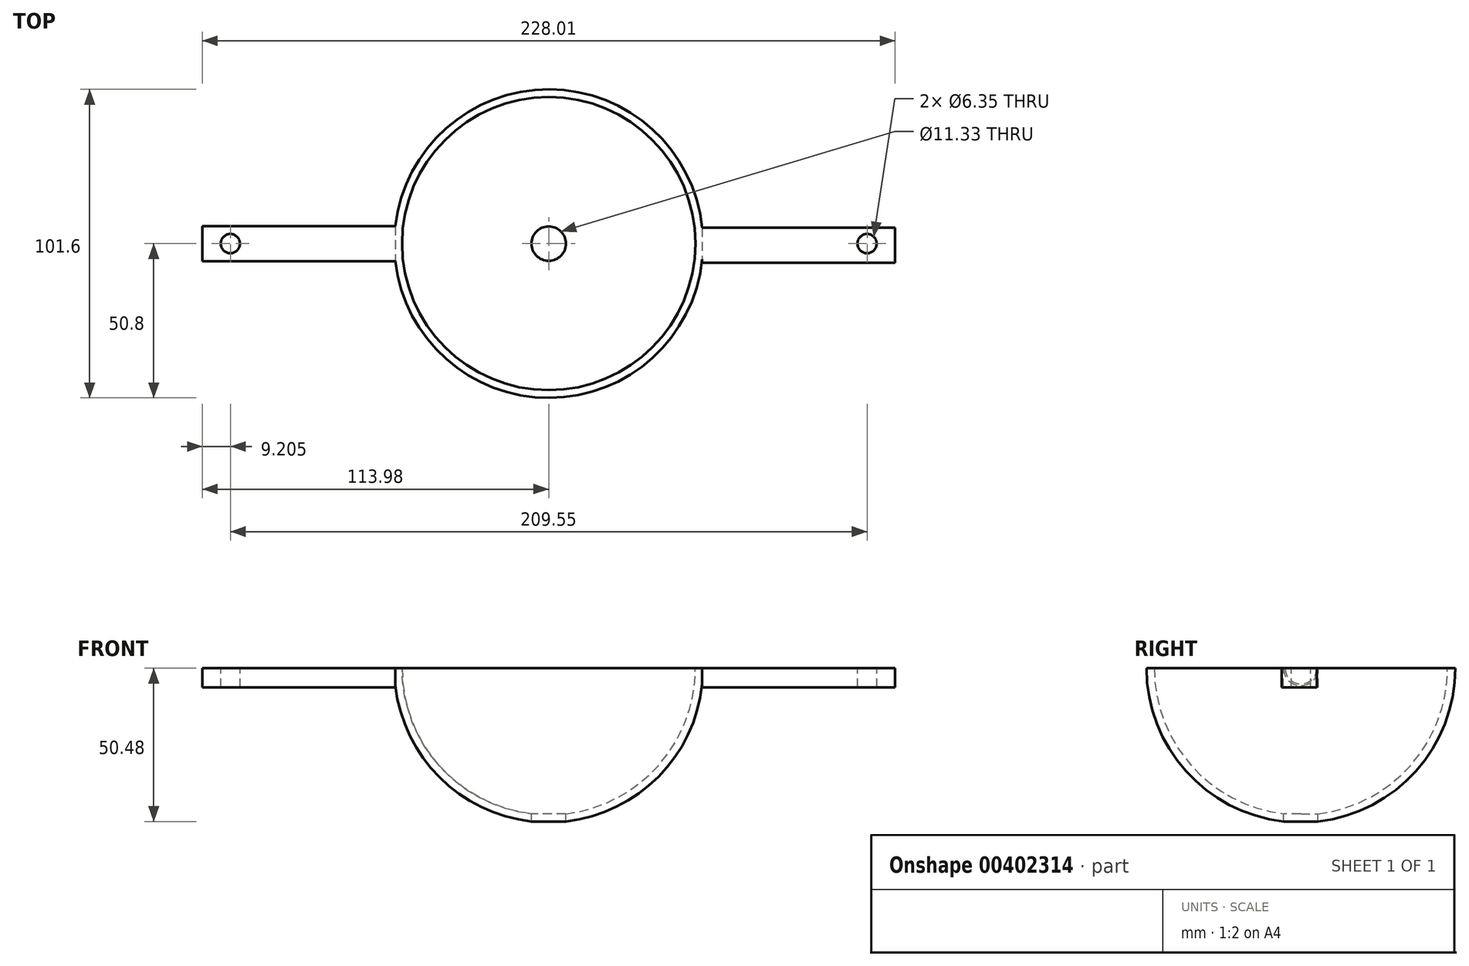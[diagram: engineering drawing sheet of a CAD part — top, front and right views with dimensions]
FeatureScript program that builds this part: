
annotation { "Feature Type Name" : "Feature", "Feature Type Description" : "" }
export const myFeature = defineFeature(function(context is Context, id is Id, definition is map)
    precondition{}
    {
        {
            var Q0;
            Q0=qCreatedBy(makeId("Front.planeOp"),FACE);
            var sketch = newSketch(context, id + "F0", { "sketchPlane" : qUnion([Q0])});
            skArc(sketch, "E0", {"start": v(-50.8, 0) * mm, "mid": v(-35.92, -35.92) * mm, "end": v(0, -50.8) * mm});
            skLineSegment(sketch, "E1", {"start": v(-50.8, 0) * mm, "end": v(0, 0) * mm});
            skLineSegment(sketch, "E2", {"start": v(0, 0) * mm, "end": v(0, -50.8) * mm});
            skPoint(sketch, "E3.orphan", {"position": v(50.8, 0) * mm});
            skSolve(sketch);
        }
        {
            var Q0;
            Q0 = qSketchRegion(id + "F0", true);
            var Q1;
            Q1=sQuery(id+"F0.wireOp",EDGE,"E2");
            revolve(context, id + "F1", {"entities" : qUnion([Q0]), "axis" : qUnion([Q1]), "revolveType" : RevolveType.FULL});
        }
        {
            var Q0;
            Q0=makeQuery(id+"F1.opRevolve","SWEPT_FACE",FACE,{"disambiguationData":[OSD([sQuery(id+"F0.wireOp",EDGE,"E1")])]});
            shell(context, id + "F2", {"entities" : qUnion([Q0]), "thickness" : 2.54 * mm});
        }
        {
            var Q0;
            Q0=qCreatedBy(makeId("Top.planeOp"),FACE);
            var sketch = newSketch(context, id + "F3", { "sketchPlane" : qUnion([Q0])});
            skCircle(sketch, "E4", {"center": v(0, 0) * mm, "radius": 5.67 * mm});
            skSolve(sketch);
        }
        {
            var Q0;
            Q0=makeQuery(id+"F3.imprint","IMPRINT",FACE,{"disambiguationData":[TD([[makeQuery(id+"F3.imprint","IMPRINT",EDGE,{"derivedFrom":sQuery(id+"F3.wireOp",EDGE,"E4")}),1.0]])]});
            extrude(context, id + "F4", {"entities" : qUnion([Q0]), "operationType" : NewBodyOperationType.REMOVE, "endBound" : BoundingType.THROUGH_ALL, "oppositeDirection" : true, "depth" : 25.4 * mm});
        }
        {
            var Q0;
            Q0=qCreatedBy(makeId("Top.planeOp"),FACE);
            var sketch = newSketch(context, id + "F5", { "sketchPlane" : qUnion([Q0])});
            skLineSegment(sketch, "E5.bottom", {"start": v(-50.48, 5.73) * mm, "end": v(-113.98, 5.73) * mm});
            skLineSegment(sketch, "E5.top", {"start": v(-50.48, -5.75) * mm, "end": v(-113.98, -5.75) * mm});
            skLineSegment(sketch, "E5.left", {"start": v(-50.48, 5.73) * mm, "end": v(-50.48, -5.75) * mm});
            skLineSegment(sketch, "E5.right", {"start": v(-113.98, 5.73) * mm, "end": v(-113.98, -5.75) * mm});
            skLineSegment(sketch, "E6", {"start": v(-113.98, 0) * mm, "end": v(-50.48, 0) * mm});
            skSolve(sketch);
        }
        {
            var Q0;
            Q0 = qSketchRegion(id + "F5", true);
            extrude(context, id + "F6", {"entities" : qUnion([Q0]), "operationType" : NewBodyOperationType.ADD, "oppositeDirection" : true, "depth" : 6.35 * mm});
        }
        {
            var Q0;
            Q0=qCreatedBy(makeId("Top.planeOp"),FACE);
            var sketch = newSketch(context, id + "F7", { "sketchPlane" : qUnion([Q0])});
            skArc(sketch, "E7.0", {"start": v(-50.48, -5.73) * mm, "mid": v(50.8, 0) * mm, "end": v(-50.48, 5.73) * mm});
            skLineSegment(sketch, "E8.bottom", {"start": v(50.53, 5.21) * mm, "end": v(114.03, 5.21) * mm});
            skLineSegment(sketch, "E8.top", {"start": v(50.53, -6.27) * mm, "end": v(114.03, -6.27) * mm});
            skLineSegment(sketch, "E8.left", {"start": v(50.53, 5.21) * mm, "end": v(50.53, -6.27) * mm});
            skLineSegment(sketch, "E8.right", {"start": v(114.03, 5.21) * mm, "end": v(114.03, -6.27) * mm});
            skLineSegment(sketch, "E9", {"start": v(50.53, -0.53) * mm, "end": v(114.03, -0.53) * mm});
            skSolve(sketch);
        }
        {
            var Q0;
            Q0 = qSketchRegion(id + "F7", true);
            extrude(context, id + "F8", {"entities" : qUnion([Q0]), "operationType" : NewBodyOperationType.ADD, "oppositeDirection" : true, "depth" : 6.35 * mm});
        }
        {
            var Q0;
            Q0=makeQuery(id+"F8.boolean.opBoolean","MERGE",FACE,{"derivedFrom":[makeQuery(id+"F6.boolean.opBoolean","MERGE",FACE,{"derivedFrom":[makeQuery(id+"F1.opRevolve","SWEPT_FACE",FACE,{"disambiguationData":[OSD([sQuery(id+"F0.wireOp",EDGE,"E1")])]}),makeQuery(id+"F6.opExtrude","CAP_FACE",FACE,{"disambiguationData":[OSD([sQuery(id+"F5.wireOp",EDGE,"E5.bottom"),sQuery(id+"F5.wireOp",EDGE,"E5.top"),sQuery(id+"F5.wireOp",EDGE,"E5.left"),sQuery(id+"F5.wireOp",EDGE,"E5.right")])],"isStart":true})]}),makeQuery(id+"F8.opExtrude","CAP_FACE",FACE,{"disambiguationData":[OSD([sQuery(id+"F7.wireOp",EDGE,"E8.bottom"),sQuery(id+"F7.wireOp",EDGE,"E8.top"),sQuery(id+"F7.wireOp",EDGE,"E8.left"),sQuery(id+"F7.wireOp",EDGE,"E8.right")])],"isStart":true})]});
            var sketch = newSketch(context, id + "F9", { "sketchPlane" : qUnion([Q0])});
            skCircle(sketch, "E10", {"center": v(-104.78, 0) * mm, "radius": 3.17 * mm});
            skCircle(sketch, "E11", {"center": v(104.78, 0) * mm, "radius": 3.18 * mm});
            skSolve(sketch);
        }
        {
            var Q0;
            Q0 = qSketchRegion(id + "F9", true);
            extrude(context, id + "F10", {"entities" : qUnion([Q0]), "operationType" : NewBodyOperationType.REMOVE, "oppositeDirection" : true, "depth" : 6.35 * mm});
        }
    });
